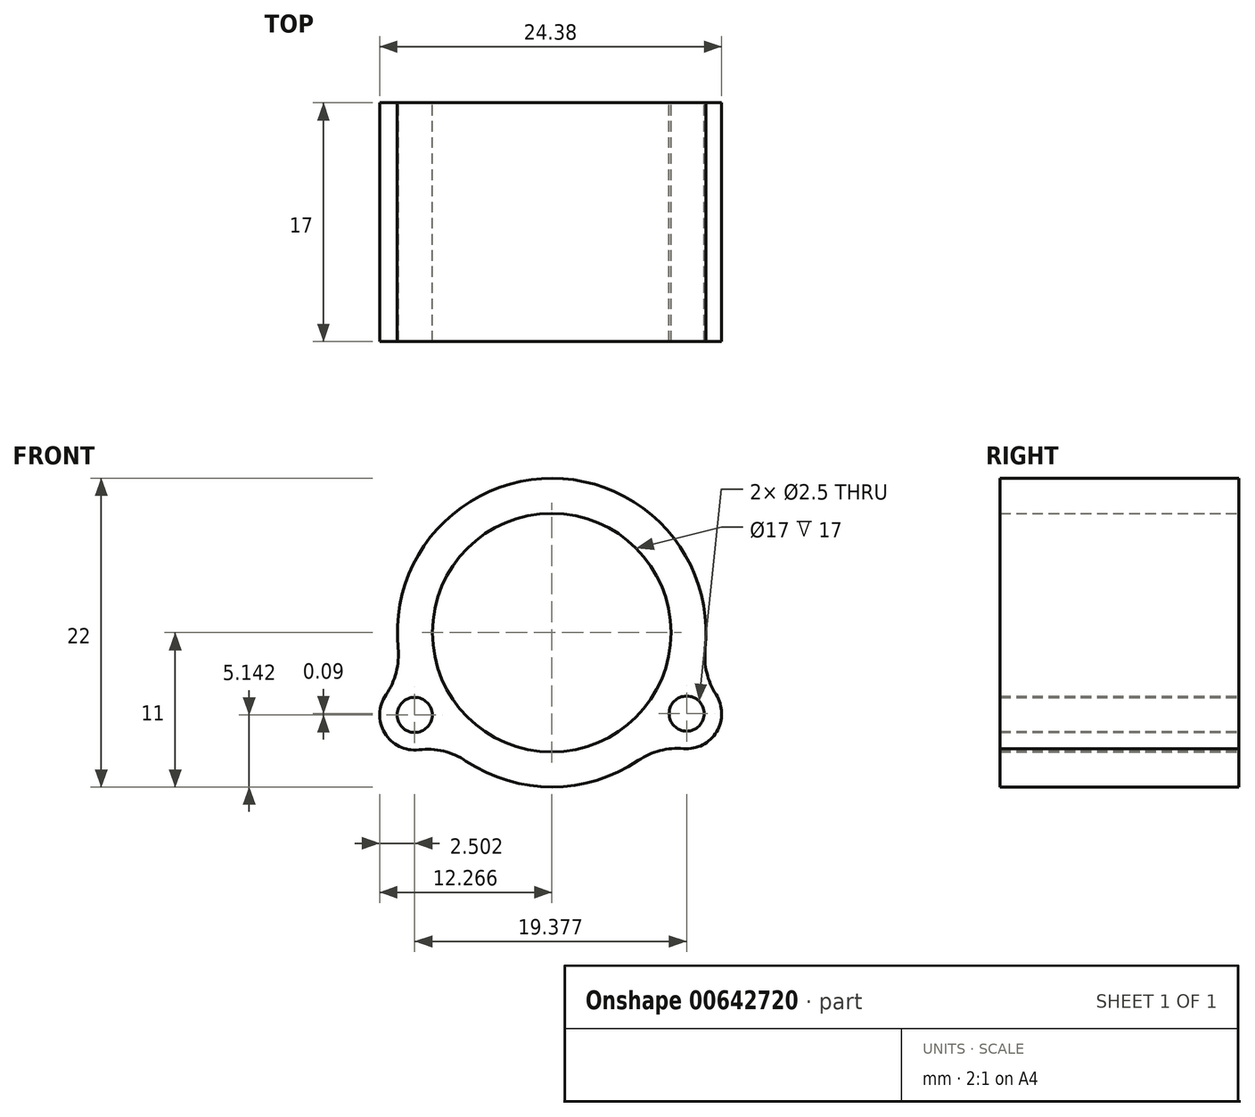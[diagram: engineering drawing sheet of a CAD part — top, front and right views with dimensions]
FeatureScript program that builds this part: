
annotation { "Feature Type Name" : "Feature", "Feature Type Description" : "" }
export const myFeature = defineFeature(function(context is Context, id is Id, definition is map)
    precondition{}
    {
        {
            var Q0;
            Q0=qCreatedBy(makeId("Front.planeOp"),FACE);
            var sketch = newSketch(context, id + "F0", { "sketchPlane" : qUnion([Q0])});
            skCircle(sketch, "E0", {"center": v(0.27, 4.78) * mm, "radius": 8.5 * mm});
            skArc(sketch, "E1", {"start": v(9.67, -3.48) * mm, "mid": v(12.02, -2.27) * mm, "end": v(11.98, 0.37) * mm});
            skArc(sketch, "E2", {"start": v(-11.55, 0.35) * mm, "mid": v(-11.64, -2.36) * mm, "end": v(-9.2, -3.56) * mm});
            skPoint(sketch, "E3.orphan", {"position": v(8.88, -0.99) * mm});
            skPoint(sketch, "E4.orphan", {"position": v(-11.17, 4.17) * mm});
            skPoint(sketch, "E5.start.orphan", {"position": v(-5.9, -1.08) * mm});
            skArc(sketch, "E6.trimOffspring", {"start": v(-5.84, -4.37) * mm, "mid": v(0.3, -6.22) * mm, "end": v(6.44, -4.32) * mm});
            skArc(sketch, "E7.trimOffspring", {"start": v(11.2, 3.62) * mm, "mid": v(0.3, 15.78) * mm, "end": v(-10.68, 3.7) * mm});
            skCircle(sketch, "E8", {"center": v(-9.5, -1.08) * mm, "radius": 1.25 * mm});
            skCircle(sketch, "E9", {"center": v(9.88, -0.99) * mm, "radius": 1.25 * mm});
            skPoint(sketch, "E10.visualSharp", {"position": v(10.72, 1.37) * mm});
            skArc(sketch, "E10.filletArc", {"start": v(11.2, 3.62) * mm, "mid": v(11.31, 1.93) * mm, "end": v(11.98, 0.37) * mm});
            skPoint(sketch, "E11.visualSharp", {"position": v(8.2, -2.84) * mm});
            skArc(sketch, "E11.filletArc", {"start": v(9.67, -3.48) * mm, "mid": v(7.98, -3.62) * mm, "end": v(6.44, -4.32) * mm});
            skPoint(sketch, "E12.visualSharp", {"position": v(-10.18, 1.33) * mm});
            skArc(sketch, "E12.filletArc", {"start": v(-11.55, 0.35) * mm, "mid": v(-10.82, 1.94) * mm, "end": v(-10.68, 3.7) * mm});
            skPoint(sketch, "E13.visualSharp", {"position": v(-7.7, -2.81) * mm});
            skArc(sketch, "E13.filletArc", {"start": v(-5.84, -4.37) * mm, "mid": v(-7.45, -3.66) * mm, "end": v(-9.2, -3.56) * mm});
            skSolve(sketch);
        }
        {
            var Q0;
            Q0 = qSketchRegion(id + "F0", true);
            extrude(context, id + "F1", {"entities" : qUnion([Q0]), "depth" : 17 * mm, "offsetDistance" : 25 * mm});
        }
    });
